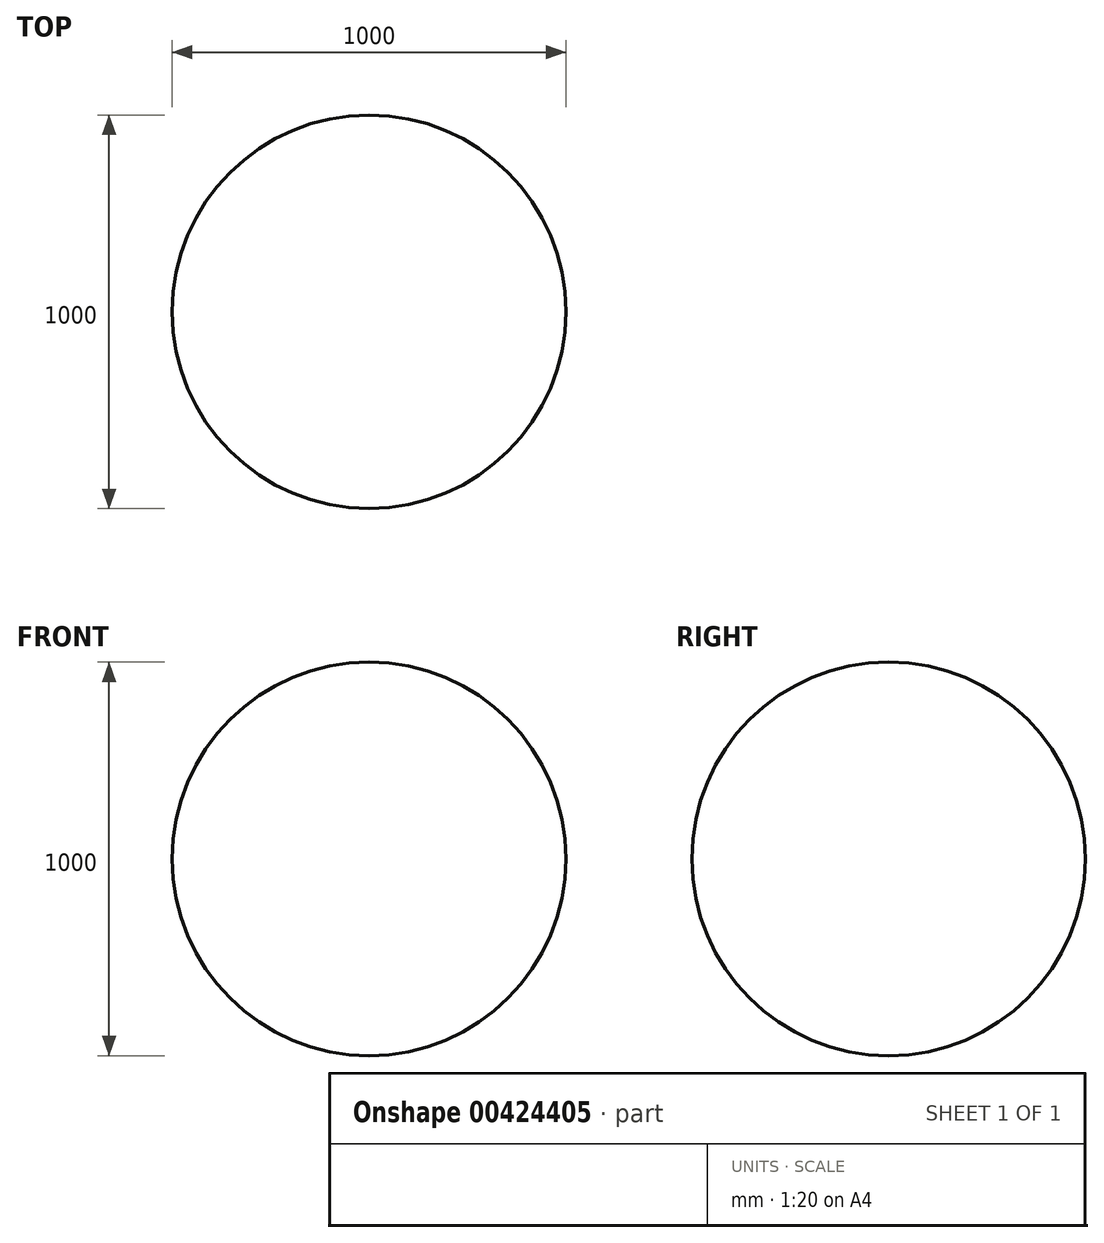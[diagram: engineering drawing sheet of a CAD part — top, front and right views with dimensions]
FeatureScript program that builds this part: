
annotation { "Feature Type Name" : "Feature", "Feature Type Description" : "" }
export const myFeature = defineFeature(function(context is Context, id is Id, definition is map)
    precondition{}
    {
        {
            var Q0;
            Q0=qCreatedBy(makeId("Front.planeOp"),FACE);
            var sketch = newSketch(context, id + "F0", { "sketchPlane" : qUnion([Q0])});
            skArc(sketch, "E0", {"start": v(500, 0) * mm, "mid": v(0, 500) * mm, "end": v(-500, 0) * mm});
            skLineSegment(sketch, "E1", {"start": v(-500, 0) * mm, "end": v(500, 0) * mm});
            skSolve(sketch);
        }
        {
            var Q0;
            Q0=sQuery(id+"F0.wireOp",EDGE,"E0");
            var Q1;
            Q1=sQuery(id+"F0.wireOp",EDGE,"E1");
            revolve(context, id + "F1", {"bodyType" : ToolBodyType.SURFACE, "surfaceEntities" : qUnion([Q0]), "axis" : qUnion([Q1]), "revolveType" : RevolveType.FULL});
        }
    });
